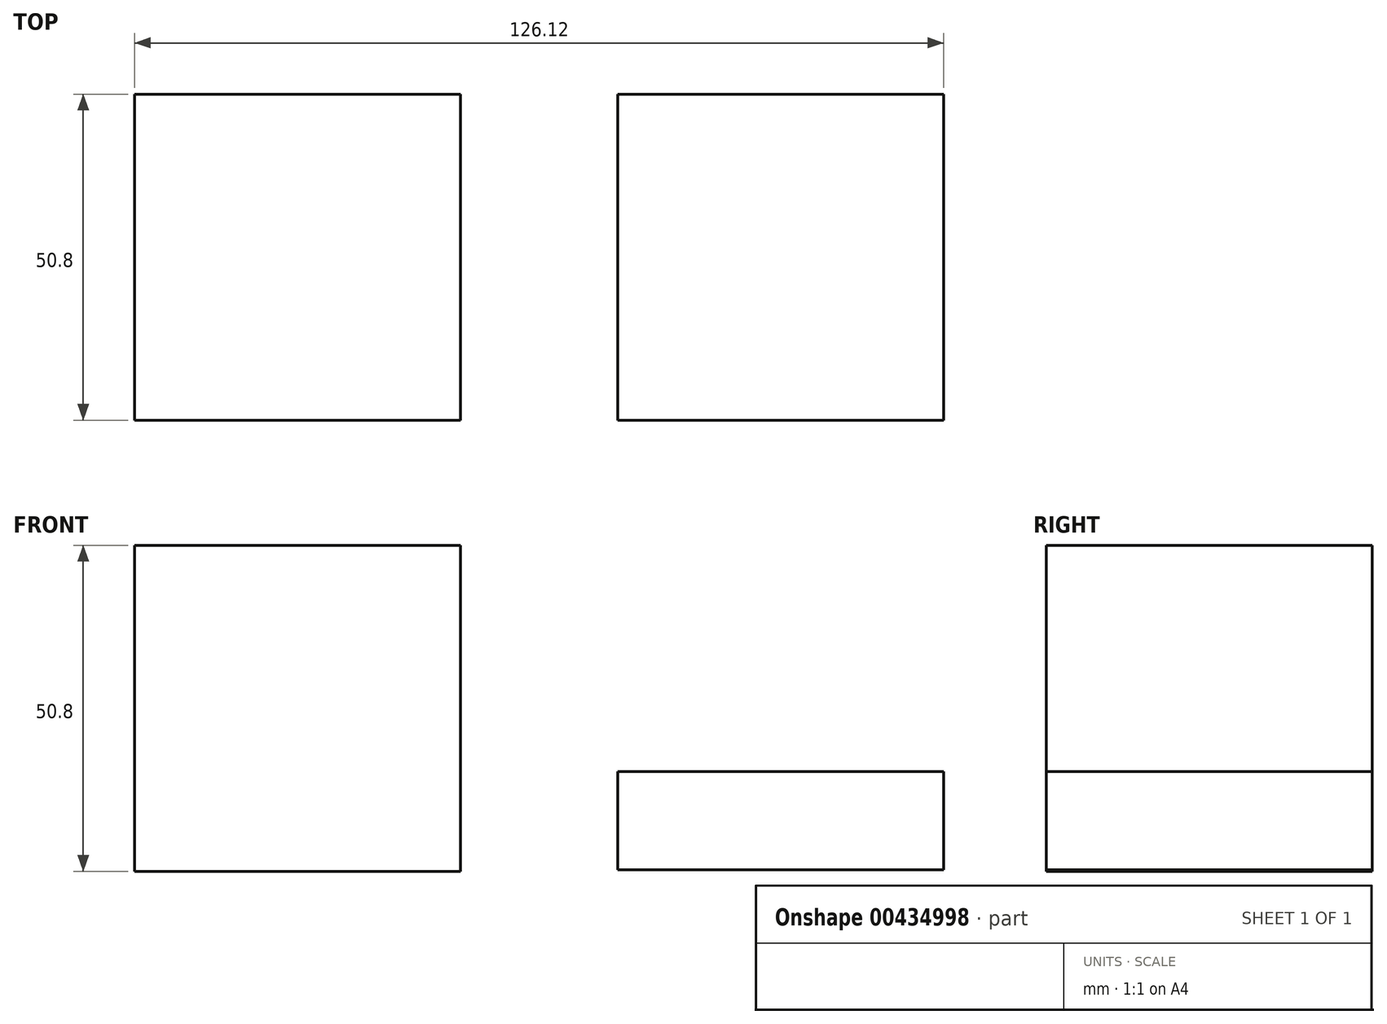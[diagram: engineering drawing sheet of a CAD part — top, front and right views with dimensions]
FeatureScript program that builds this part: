
annotation { "Feature Type Name" : "Feature", "Feature Type Description" : "" }
export const myFeature = defineFeature(function(context is Context, id is Id, definition is map)
    precondition{}
    {
        {
            var Q0;
            Q0=qCreatedBy(makeId("Front.planeOp"),FACE);
            var sketch = newSketch(context, id + "F0", { "sketchPlane" : qUnion([Q0])});
            skLineSegment(sketch, "E0.bottom", {"start": v(-66.08, 74) * mm, "end": v(-15.28, 74) * mm});
            skLineSegment(sketch, "E0.top", {"start": v(-66.08, 23.2) * mm, "end": v(-15.28, 23.2) * mm});
            skLineSegment(sketch, "E0.left", {"start": v(-66.08, 74) * mm, "end": v(-66.08, 23.2) * mm});
            skLineSegment(sketch, "E0.right", {"start": v(-15.28, 74) * mm, "end": v(-15.28, 23.2) * mm});
            skLineSegment(sketch, "E1.bottom", {"start": v(10.6, 39.33) * mm, "end": v(61.4, 39.33) * mm});
            skLineSegment(sketch, "E1.top", {"start": v(10.6, 13.93) * mm, "end": v(61.4, 13.93) * mm});
            skLineSegment(sketch, "E1.left", {"start": v(10.6, 39.33) * mm, "end": v(10.6, 13.93) * mm});
            skLineSegment(sketch, "E1.right", {"start": v(61.4, 39.33) * mm, "end": v(61.4, 13.93) * mm});
            skCircle(sketch, "E2", {"center": v(-44.13, -28.48) * mm, "radius": 25.4 * mm});
            skSolve(sketch);
        }
        {
            var Q0;
            Q0=makeQuery(id+"F0.imprint","IMPRINT",FACE,{"disambiguationData":[TD([[makeQuery(id+"F0.imprint","IMPRINT",EDGE,{"derivedFrom":sQuery(id+"F0.wireOp",EDGE,"E0.bottom")}),-1.0]])]});
            extrude(context, id + "F1", {"entities" : qUnion([Q0]), "depth" : 50.8 * mm});
        }
        {
            var Q0;
            Q0=qCreatedBy(makeId("Front.planeOp"),FACE);
            var sketch = newSketch(context, id + "F2", { "sketchPlane" : qUnion([Q0])});
            skLineSegment(sketch, "E3.bottom", {"start": v(9.24, 38.75) * mm, "end": v(60.04, 38.75) * mm});
            skLineSegment(sketch, "E3.top", {"start": v(9.24, 23.39) * mm, "end": v(60.04, 23.39) * mm});
            skLineSegment(sketch, "E3.left", {"start": v(9.24, 38.75) * mm, "end": v(9.24, 23.39) * mm});
            skLineSegment(sketch, "E3.right", {"start": v(60.04, 38.75) * mm, "end": v(60.04, 23.39) * mm});
            skSolve(sketch);
        }
        {
            var Q0;
            Q0=makeQuery(id+"F2.imprint","IMPRINT",FACE,{"disambiguationData":[TD([[makeQuery(id+"F2.imprint","IMPRINT",EDGE,{"derivedFrom":sQuery(id+"F2.wireOp",EDGE,"E3.bottom")}),-1.0]])]});
            extrude(context, id + "F3", {"entities" : qUnion([Q0]), "depth" : 50.8 * mm});
        }
    });
